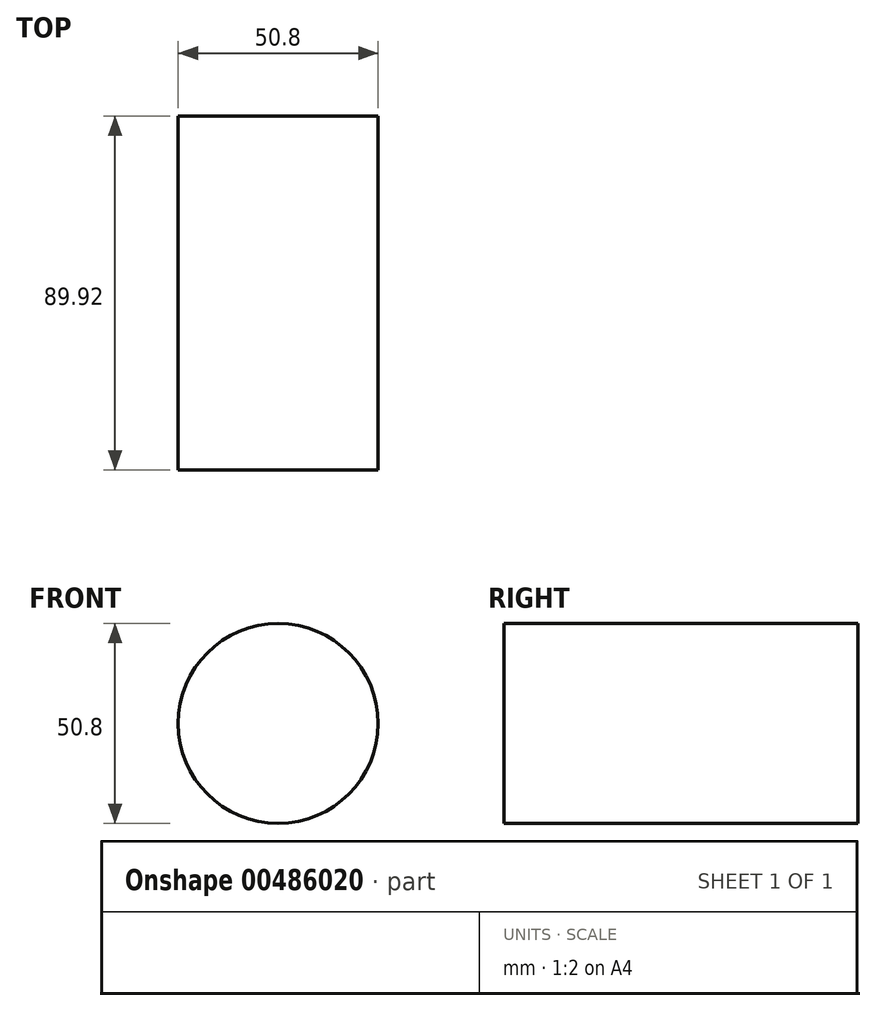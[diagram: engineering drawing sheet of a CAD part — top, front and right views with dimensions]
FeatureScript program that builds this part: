
annotation { "Feature Type Name" : "Feature", "Feature Type Description" : "" }
export const myFeature = defineFeature(function(context is Context, id is Id, definition is map)
    precondition{}
    {
        {
            var Q0;
            Q0=qCreatedBy(makeId("Front.planeOp"),FACE);
            var sketch = newSketch(context, id + "F0", { "sketchPlane" : qUnion([Q0])});
            skCircle(sketch, "E0", {"center": v(0, 0) * mm, "radius": 25.4 * mm});
            skSolve(sketch);
        }
        {
            var Q0;
            Q0=qSketchRegion(id+"F0",true);
            extrude(context, id + "F1", {"entities" : qUnion([Q0]), "depth" : 89.92 * mm});
        }
    });
